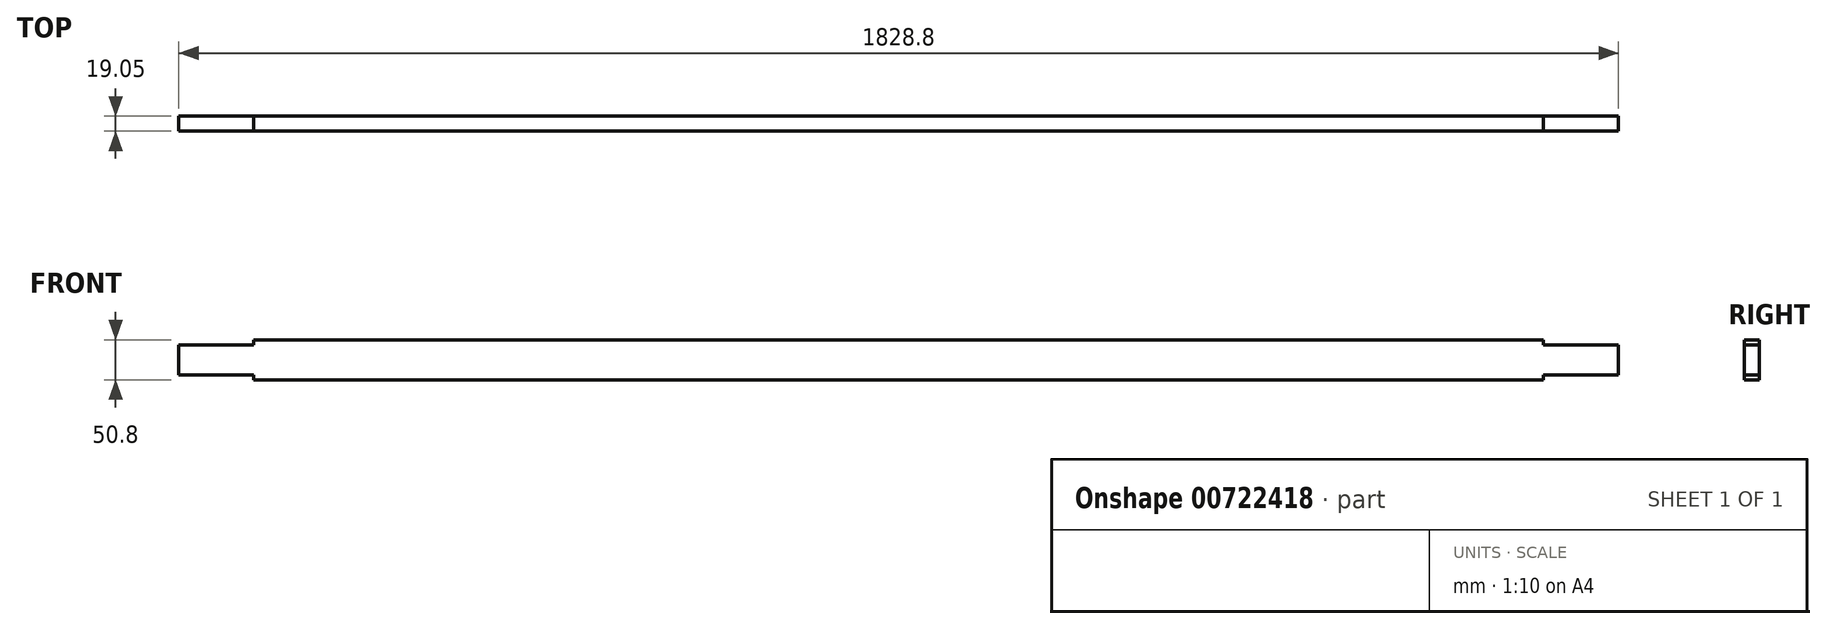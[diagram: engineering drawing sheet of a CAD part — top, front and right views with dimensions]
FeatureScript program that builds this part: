
annotation { "Feature Type Name" : "Feature", "Feature Type Description" : "" }
export const myFeature = defineFeature(function(context is Context, id is Id, definition is map)
    precondition{}
    {
        {
            var Q0;
            Q0=qCreatedBy(makeId("Front.planeOp"),FACE);
            var sketch = newSketch(context, id + "F0", { "sketchPlane" : qUnion([Q0])});
            skLineSegment(sketch, "E0.bottom", {"start": v(914.4, -25.4) * mm, "end": v(-914.4, -25.4) * mm});
            skLineSegment(sketch, "E0.top", {"start": v(914.4, 25.4) * mm, "end": v(-914.4, 25.4) * mm});
            skLineSegment(sketch, "E0.left", {"start": v(914.4, -25.4) * mm, "end": v(914.4, 25.4) * mm});
            skLineSegment(sketch, "E0.right", {"start": v(-914.4, -25.4) * mm, "end": v(-914.4, 25.4) * mm});
            skPoint(sketch, "E0.middle", {"position": v(0, 0) * mm});
            skLineSegment(sketch, "E1.bottom", {"start": v(-914.4, 25.4) * mm, "end": v(-819.15, 25.4) * mm});
            skLineSegment(sketch, "E1.top", {"start": v(-914.4, 19.05) * mm, "end": v(-819.15, 19.05) * mm});
            skLineSegment(sketch, "E1.left", {"start": v(-914.4, 25.4) * mm, "end": v(-914.4, 19.05) * mm});
            skLineSegment(sketch, "E1.right", {"start": v(-819.15, 25.4) * mm, "end": v(-819.15, 19.05) * mm});
            skLineSegment(sketch, "E2.bottom", {"start": v(-914.4, -25.4) * mm, "end": v(-819.15, -25.4) * mm});
            skLineSegment(sketch, "E2.top", {"start": v(-914.4, -19.05) * mm, "end": v(-819.15, -19.05) * mm});
            skLineSegment(sketch, "E2.left", {"start": v(-914.4, -25.4) * mm, "end": v(-914.4, -19.05) * mm});
            skLineSegment(sketch, "E2.right", {"start": v(-819.15, -25.4) * mm, "end": v(-819.15, -19.05) * mm});
            skLineSegment(sketch, "E3.bottom", {"start": v(914.4, -25.4) * mm, "end": v(819.15, -25.4) * mm});
            skLineSegment(sketch, "E3.top", {"start": v(914.4, -19.05) * mm, "end": v(819.15, -19.05) * mm});
            skLineSegment(sketch, "E3.left", {"start": v(914.4, -25.4) * mm, "end": v(914.4, -19.05) * mm});
            skLineSegment(sketch, "E3.right", {"start": v(819.15, -25.4) * mm, "end": v(819.15, -19.05) * mm});
            skLineSegment(sketch, "E4.bottom", {"start": v(914.4, 25.4) * mm, "end": v(819.15, 25.4) * mm});
            skLineSegment(sketch, "E4.top", {"start": v(914.4, 19.05) * mm, "end": v(819.15, 19.05) * mm});
            skLineSegment(sketch, "E4.left", {"start": v(914.4, 25.4) * mm, "end": v(914.4, 19.05) * mm});
            skLineSegment(sketch, "E4.right", {"start": v(819.15, 25.4) * mm, "end": v(819.15, 19.05) * mm});
            skSolve(sketch);
        }
        {
            var Q0;
            {var subQ3=sQuery(id+"F0.wireOp",EDGE,"E1.top");Q0=makeQuery(id+"F0.imprint","IMPRINT",FACE,{"disambiguationData":[TD([[makeQuery(id+"F0.imprint","IMPRINT",EDGE,{"derivedFrom":subQ3}),-1.0]])]});}
            extrude(context, id + "F1", {"entities" : qUnion([Q0]), "depth" : 19.05 * mm, "offsetDistance" : 25.4 * mm});
        }
    });
